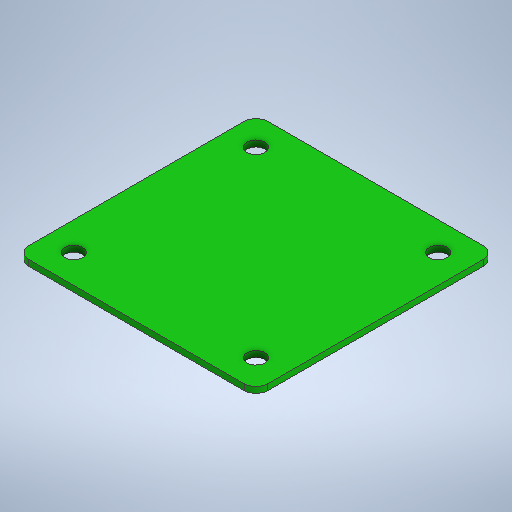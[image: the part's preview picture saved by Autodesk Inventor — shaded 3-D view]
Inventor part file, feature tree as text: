
AUTODESK INVENTOR PART (.ipt)
format: ipt  version: 2025.2 (Build 292293000, 293)  size: 249,856 bytes
history: native  units: in
note: dims shown in document units (in); Inventor stores cm internally (conversion verified against a paired STEP export)
features: extrude x1, fillet x1, sketch x1
ambient origin geometry x8: Origin, YZ Plane, XZ Plane, XY Plane, X Axis, Y Axis, Z Axis, Center Point
bodies: Solid1 (feature_tree)
feature tree (3):
  extrude  "Extrusion1"  Depth=1.5748in
  fillet  "Fillet1"  Radius=0.1181in
  sketch  "Sketch1"  dims[d0=1.5748in d1=1.5748in d2=0.1181in d3=0.1181in d4=0.1181in d5=0.1181in d6=1.2008in d7=1.2008in d8=1.2008in d9=1.2008in d10=0.6004in d11=0.6004in d12=0.6004in d13=0.6004in d14=0.0394in d15=0.0in d16=0.0787in]
